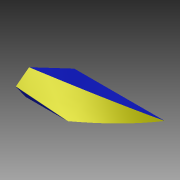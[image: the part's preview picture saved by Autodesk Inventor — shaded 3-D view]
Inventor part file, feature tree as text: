
AUTODESK INVENTOR PART (.ipt)
format: ipt  version: 2014 (Build 180170000, 170)  size: 516,096 bytes
history: native  units: in
note: dims shown in document units (in); Inventor stores cm internally (conversion verified against a paired STEP export)
features: sketch x22, extrude x15, plane x9, loft x4, projected_geometry x4, other x3, mirror x1, emboss x1
ambient origin geometry x8: Origin, YZ Plane, XZ Plane, XY Plane, X Axis, Y Axis, Z Axis, Center Point
bodies: Solid1 (feature_tree)
feature tree (59):
  sketch  "Sketch1"  dims[d0=0.7559in d1=0.7559in]
  plane  "Work Plane1"
  loft  "Loft1"
  extrude  "Extrusion1"  Depth=0.2in
  plane  "Work Plane4"
  loft  "Loft2"
  plane  "Work Plane5"
  loft  "Loft3"
  loft  "Loft4"
  extrude  "Extrusion2"  TaperAngle=0.0deg  [1 undecoded]
  plane  "Work Plane6"
  extrude  "Extrusion3"  Depth=1.0in
  extrude  "Extrusion4"  Depth=1.0651in
  extrude  "Extrusion5"  Depth=0.962in
  plane  "Work Plane7"
  extrude  "Extrusion6"  Depth=0.075in
  plane  "Work Plane8"
  other  "Work Axis1"
  plane  "Work Plane9"
  extrude  "Extrusion7"  Depth=0.06in
  mirror  "Mirror3"
  extrude  "Extrusion8"  Depth=0.05in
  plane  "Work Plane10"
  extrude  "Extrusion9"  Depth=0.0625in
  plane  "Work Plane11"
  extrude  "Extrusion10"  Depth=0.075in
  extrude  "Extrusion11"  TaperAngle=0.0deg  [1 undecoded]
  extrude  "Extrusion12"  Depth=0.2in
  extrude  "Extrusion13"  TaperAngle=0.0deg  [1 undecoded]
  emboss  "Emboss1"
  extrude  "Extrusion15"  Depth=0.01in
  extrude  "Extrusion16"  Depth=0.0344in
  sketch  "Sketch2"  dims[d2=0.9963in d3=0.2in]
  sketch  "Sketch3"  dims[d4=0.5in d6=0.08in]
  sketch  "Sketch4"  dims[d7=0.55in d8=150.0deg]
  other  "Edges1"
  sketch  "Sketch5"  dims[d9=150.0deg d14=0.33in]
  projected_geometry  "Projected Loop1"
  other  "Edges2"
  sketch  "Sketch6"  dims[d15=0.66in d18=0.0in d19=90.0deg]
  sketch  "Sketch7"  dims[d20=0.0in d21=90.0deg d22=1.0in]
  sketch  "Sketch8"  dims[d26=1.0651in d28=1.0651in]
  sketch  "Sketch9"  dims[d29=0.0in d30=0.962in]
  sketch  "Sketch10"  dims[d31=0.962in d32=0.075in]
  sketch  "Sketch11"  dims[d33=0.15in d34=0.06in]
  sketch  "Sketch12"  dims[d35=0.1in d36=0.05in]
  sketch  "Sketch13"  dims[d37=0.45in d38=0.0in d39=0.0625in]
  projected_geometry  "Projected Loop2"
  projected_geometry  "Projected Loop3"
  sketch  "Sketch14"  dims[d40=0.01in d41=0.075in]
  projected_geometry  "Projected Loop4"
  sketch  "Sketch15"  dims[d42=0.01in d43=0.0in d44=90.0deg]
  sketch  "Sketch16"  dims[d45=0.0in d46=90.0deg d47=0.2in]
  sketch  "Sketch17"  dims[d48=0.07in d49=0.0in d50=90.0deg]
  sketch  "Sketch18"  dims[d51=0.0in d52=90.0deg d53=0.01in]
  sketch  "Sketch19"  dims[d54=0.01in d55=0.0344in]
  sketch  "Sketch20"  dims[d56=150.0deg]
  sketch  "Sketch22"  dims[d57=60.0deg]
  sketch  "Sketch23"  dims[d58=150.0deg d59=0.7in d60=0.05in d61=0.05in d62=0.05in d63=0.05in d64=0.05in d65=0.01in d66=0.0in d67=90.0deg d68=0.0in d69=90.0deg d70=0.1in d71=0.4in d72=0.15in d73=0.05in d74=0.0in d75=0.02in d77=0.15in d78=0.02in d79=0.1in d80=0.1in d81=0.1in d82=0.02in d83=0.15in d84=0.05in d85=0.0in d86=0.045in d87=0.0in d88=0.025in d89=0.0in d90=0.02in d91=0.02in d92=0.005in d93=0.0in d94=90.0deg d95=0.4466in d96=1.0in d97=0.0in d98=1.0in d99=0.0in d100=0.6528in d101=0.0in d102=0.0in d103=1.0in d104=0.0in d106=90.0deg d107=1.0in d108=0.0in d109=1.65in d110=0.1in d111=0.075in d112=0.0in d113=0.1in d114=0.075in d115=0.0in d116=0.05in d117=0.0in d121=1.0in d122=0.0in d123=1.0in d124=0.0in]
note: 3 required parameter values undecoded (feature->parameter linkage not recoverable at this tier; creation-order binding heuristic only, values carry confidence <= 0.55)
